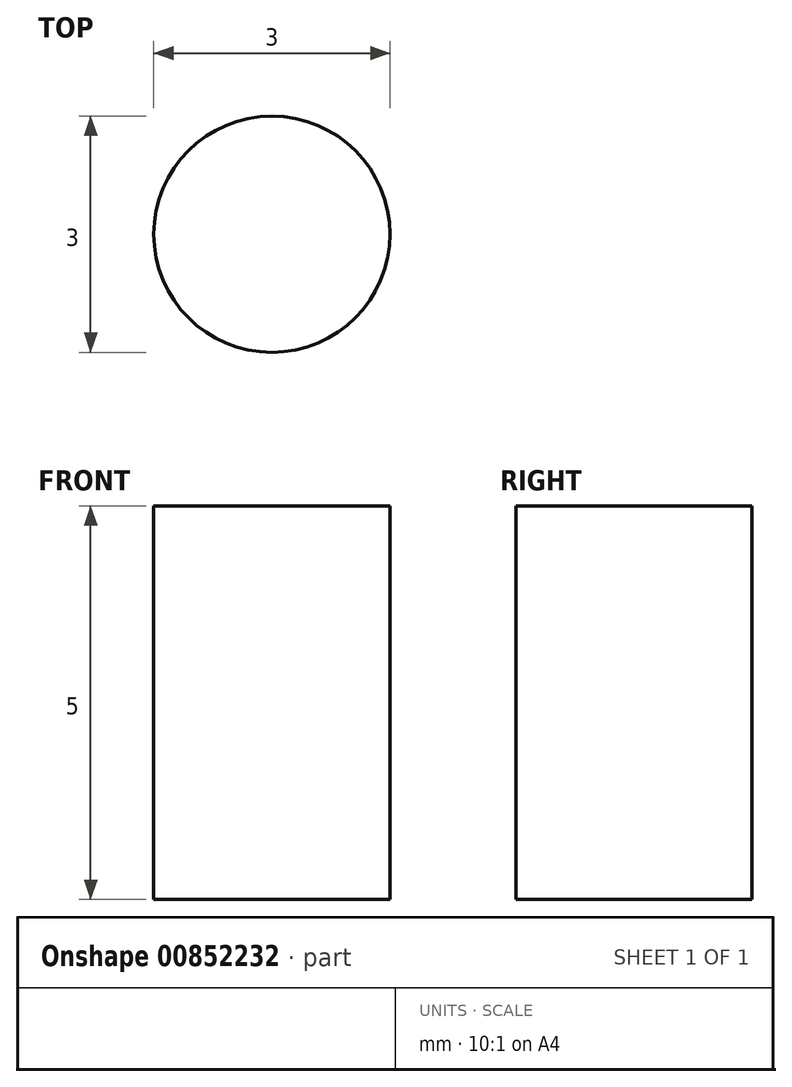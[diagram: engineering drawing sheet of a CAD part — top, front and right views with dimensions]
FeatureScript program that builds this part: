
annotation { "Feature Type Name" : "Feature", "Feature Type Description" : "" }
export const myFeature = defineFeature(function(context is Context, id is Id, definition is map)
    precondition{}
    {
        {
            var Q0;
            Q0=qCreatedBy(makeId("Top.planeOp"),FACE);
            var sketch = newSketch(context, id + "F0", { "sketchPlane" : qUnion([Q0])});
            skCircle(sketch, "E0", {"center": v(0, 0) * mm, "radius": 27 * mm});
            skSolve(sketch);
        }
        {
            var Q0;
            Q0=makeQuery(id+"F0.imprint","IMPRINT",FACE,{"disambiguationData":[TD([[makeQuery(id+"F0.imprint","IMPRINT",EDGE,{"derivedFrom":sQuery(id+"F0.wireOp",EDGE,"E0")}),1.0]])]});
            extrude(context, id + "F1", {"entities" : qUnion([Q0]), "depth" : 5 * mm, "offsetDistance" : 25 * mm});
        }
        {
            var Q0;
            {var subQ0=sQuery(id+"F37MvCQ3r0wqFin_1.wireOp",EDGE,"f4uybqiO-2By2-jBmk-46SA-pqxdGsBmxj9X");var subQ1=sQuery(id+"F37MvCQ3r0wqFin_1.wireOp",EDGE,"YBS4xQga-kdXz-Xd6Z-IQxe-r2HOvKNWWecW");var subQ3=sQuery(id+"F37MvCQ3r0wqFin_1.wireOp",EDGE,"gupYa68e-aYtB-tSWe-53kB-uYkL865cLbxZ");var subQ4=sQuery(id+"F37MvCQ3r0wqFin_1.wireOp",EDGE,"4d4407c7-a204-4c44-b440-6ebbf1cd7b63.1.0.0");var subQ5=sQuery(id+"F0.wireOp",EDGE,"E0");var subQ6=sQuery(id+"F37MvCQ3r0wqFin_1.wireOp",EDGE,"S5JysFVE-GN5k-qked-gyNs-9rrJIgPoBisO");var subQ8=sQuery(id+"F37MvCQ3r0wqFin_1.wireOp",EDGE,"622e7514-f5f2-47ed-ba9b-ec6ca30ba75c0.MirrorCS");var subQ10=sQuery(id+"F37MvCQ3r0wqFin_1.wireOp",EDGE,"19809d41-3397-4dab-8baa-fab7fa50255a0.MirrorCS");Q0=makeQuery(id+"FV6EzTKN9YXR9Vd_1.boolean.opBoolean","SPLIT",EDGE,{"disambiguationData":[TD([makeQuery(id+"F1.opExtrude","SWEPT_FACE",FACE,{"disambiguationData":[OSD([subQ5])]}),makeQuery(id+"F1.opExtrude","CAP_FACE",FACE,{"disambiguationData":[OSD([subQ5])],"isStart":false}),makeQuery(id+"FV6EzTKN9YXR9Vd_1.opExtrude","SWEPT_FACE",FACE,{"disambiguationData":[OSD([subQ1]),TDD([makeQuery(id+"F37MvCQ3r0wqFin_1.imprint","IMPRINT",EDGE,{"disambiguationData":[TD([[makeQuery(id+"F37MvCQ3r0wqFin_1.imprint","INTERSECT",VERTEX,{"disambiguationData":[OD(0.0)],"derivedFrom":[subQ1,subQ10]}),1.0]])],"derivedFrom":subQ1})])]}),makeQuery(id+"FV6EzTKN9YXR9Vd_1.opExtrude","SWEPT_FACE",FACE,{"disambiguationData":[OSD([subQ1]),TDD([makeQuery(id+"F37MvCQ3r0wqFin_1.imprint","IMPRINT",EDGE,{"disambiguationData":[TD([[makeQuery(id+"F37MvCQ3r0wqFin_1.imprint","INTERSECT",VERTEX,{"disambiguationData":[OD(0.0)],"derivedFrom":[subQ1,subQ8]}),1.0]])],"derivedFrom":subQ1})])]}),makeQuery(id+"FV6EzTKN9YXR9Vd_1.opExtrude","SWEPT_FACE",FACE,{"disambiguationData":[OSD([subQ1]),TDD([makeQuery(id+"F37MvCQ3r0wqFin_1.imprint","IMPRINT",EDGE,{"disambiguationData":[TD([[makeQuery(id+"F37MvCQ3r0wqFin_1.imprint","INTERSECT",VERTEX,{"disambiguationData":[OD(0.0)],"derivedFrom":[subQ1,subQ6]}),1.0]])],"derivedFrom":subQ1})])]}),makeQuery(id+"FV6EzTKN9YXR9Vd_1.opExtrude","SWEPT_FACE",FACE,{"disambiguationData":[OSD([subQ1]),TDD([makeQuery(id+"F37MvCQ3r0wqFin_1.imprint","IMPRINT",EDGE,{"disambiguationData":[TD([[makeQuery(id+"F37MvCQ3r0wqFin_1.imprint","INTERSECT",VERTEX,{"disambiguationData":[OD(0.0)],"derivedFrom":[subQ1,subQ0]}),-1.0]])],"derivedFrom":subQ1})])]}),makeQuery(id+"FV6EzTKN9YXR9Vd_1.opExtrude","SWEPT_FACE",FACE,{"disambiguationData":[OSD([subQ1]),TDD([makeQuery(id+"F37MvCQ3r0wqFin_1.imprint","IMPRINT",EDGE,{"disambiguationData":[TD([[makeQuery(id+"F37MvCQ3r0wqFin_1.imprint","INTERSECT",VERTEX,{"disambiguationData":[OD(0.0)],"derivedFrom":[subQ1,subQ3]}),-1.0]])],"derivedFrom":subQ1})])]}),makeQuery(id+"FV6EzTKN9YXR9Vd_1.opExtrude","SWEPT_FACE",FACE,{"disambiguationData":[OSD([subQ1]),TDD([makeQuery(id+"F37MvCQ3r0wqFin_1.imprint","IMPRINT",EDGE,{"disambiguationData":[TD([[makeQuery(id+"F37MvCQ3r0wqFin_1.imprint","INTERSECT",VERTEX,{"disambiguationData":[OD(1.0)],"derivedFrom":[subQ1,subQ3]}),1.0]])],"derivedFrom":subQ1})])]}),makeQuery(id+"FV6EzTKN9YXR9Vd_1.opExtrude","SWEPT_FACE",FACE,{"disambiguationData":[OSD([subQ1]),TDD([makeQuery(id+"F37MvCQ3r0wqFin_1.imprint","IMPRINT",EDGE,{"disambiguationData":[TD([[makeQuery(id+"F37MvCQ3r0wqFin_1.imprint","INTERSECT",VERTEX,{"disambiguationData":[OD(1.0)],"derivedFrom":[subQ1,subQ0]}),1.0]])],"derivedFrom":subQ1})])]}),makeQuery(id+"FV6EzTKN9YXR9Vd_1.opExtrude","SWEPT_FACE",FACE,{"disambiguationData":[OSD([subQ1]),TDD([makeQuery(id+"F37MvCQ3r0wqFin_1.imprint","IMPRINT",EDGE,{"disambiguationData":[TD([[makeQuery(id+"F37MvCQ3r0wqFin_1.imprint","INTERSECT",VERTEX,{"disambiguationData":[OD(1.0)],"derivedFrom":[subQ1,subQ6]}),-1.0]])],"derivedFrom":subQ1})])]}),makeQuery(id+"FV6EzTKN9YXR9Vd_1.opExtrude","SWEPT_FACE",FACE,{"disambiguationData":[OSD([subQ1]),TDD([makeQuery(id+"F37MvCQ3r0wqFin_1.imprint","IMPRINT",EDGE,{"disambiguationData":[TD([[makeQuery(id+"F37MvCQ3r0wqFin_1.imprint","INTERSECT",VERTEX,{"disambiguationData":[OD(1.0)],"derivedFrom":[subQ1,subQ8]}),-1.0]])],"derivedFrom":subQ1})])]}),makeQuery(id+"FV6EzTKN9YXR9Vd_1.opExtrude","SWEPT_FACE",FACE,{"disambiguationData":[OSD([subQ1]),TDD([makeQuery(id+"F37MvCQ3r0wqFin_1.imprint","IMPRINT",EDGE,{"disambiguationData":[TD([[makeQuery(id+"F37MvCQ3r0wqFin_1.imprint","INTERSECT",VERTEX,{"disambiguationData":[OD(1.0)],"derivedFrom":[subQ1,subQ10]}),-1.0]])],"derivedFrom":subQ1})])]}),makeQuery(id+"FV6EzTKN9YXR9Vd_1.opExtrude","SWEPT_FACE",FACE,{"disambiguationData":[OSD([subQ4])]})])],"derivedFrom":makeQuery(id+"F1.opExtrude","CAP_EDGE",EDGE,{"disambiguationData":[OSD([subQ5])],"isStart":false})});}
            var Q1;
            {var subQ0=sQuery(id+"F37MvCQ3r0wqFin_1.wireOp",EDGE,"f4uybqiO-2By2-jBmk-46SA-pqxdGsBmxj9X");var subQ1=sQuery(id+"F37MvCQ3r0wqFin_1.wireOp",EDGE,"YBS4xQga-kdXz-Xd6Z-IQxe-r2HOvKNWWecW");var subQ2=sQuery(id+"F37MvCQ3r0wqFin_1.wireOp",EDGE,"x8pBDlyB-b0kH-kFwn-oj1M-qMSimfXZpj5B");var subQ3=sQuery(id+"F37MvCQ3r0wqFin_1.wireOp",EDGE,"gupYa68e-aYtB-tSWe-53kB-uYkL865cLbxZ");var subQ5=sQuery(id+"F0.wireOp",EDGE,"E0");var subQ6=sQuery(id+"F37MvCQ3r0wqFin_1.wireOp",EDGE,"S5JysFVE-GN5k-qked-gyNs-9rrJIgPoBisO");var subQ8=sQuery(id+"F37MvCQ3r0wqFin_1.wireOp",EDGE,"622e7514-f5f2-47ed-ba9b-ec6ca30ba75c0.MirrorCS");var subQ10=sQuery(id+"F37MvCQ3r0wqFin_1.wireOp",EDGE,"19809d41-3397-4dab-8baa-fab7fa50255a0.MirrorCS");Q1=makeQuery(id+"FV6EzTKN9YXR9Vd_1.boolean.opBoolean","SPLIT",EDGE,{"disambiguationData":[TD([makeQuery(id+"F1.opExtrude","SWEPT_FACE",FACE,{"disambiguationData":[OSD([subQ5])]}),makeQuery(id+"F1.opExtrude","CAP_FACE",FACE,{"disambiguationData":[OSD([subQ5])],"isStart":false}),makeQuery(id+"FV6EzTKN9YXR9Vd_1.opExtrude","SWEPT_FACE",FACE,{"disambiguationData":[OSD([subQ1]),TDD([makeQuery(id+"F37MvCQ3r0wqFin_1.imprint","IMPRINT",EDGE,{"disambiguationData":[TD([[makeQuery(id+"F37MvCQ3r0wqFin_1.imprint","INTERSECT",VERTEX,{"disambiguationData":[OD(0.0)],"derivedFrom":[subQ1,subQ10]}),1.0]])],"derivedFrom":subQ1})])]}),makeQuery(id+"FV6EzTKN9YXR9Vd_1.opExtrude","SWEPT_FACE",FACE,{"disambiguationData":[OSD([subQ1]),TDD([makeQuery(id+"F37MvCQ3r0wqFin_1.imprint","IMPRINT",EDGE,{"disambiguationData":[TD([[makeQuery(id+"F37MvCQ3r0wqFin_1.imprint","INTERSECT",VERTEX,{"disambiguationData":[OD(0.0)],"derivedFrom":[subQ1,subQ8]}),1.0]])],"derivedFrom":subQ1})])]}),makeQuery(id+"FV6EzTKN9YXR9Vd_1.opExtrude","SWEPT_FACE",FACE,{"disambiguationData":[OSD([subQ1]),TDD([makeQuery(id+"F37MvCQ3r0wqFin_1.imprint","IMPRINT",EDGE,{"disambiguationData":[TD([[makeQuery(id+"F37MvCQ3r0wqFin_1.imprint","INTERSECT",VERTEX,{"disambiguationData":[OD(0.0)],"derivedFrom":[subQ1,subQ6]}),1.0]])],"derivedFrom":subQ1})])]}),makeQuery(id+"FV6EzTKN9YXR9Vd_1.opExtrude","SWEPT_FACE",FACE,{"disambiguationData":[OSD([subQ1]),TDD([makeQuery(id+"F37MvCQ3r0wqFin_1.imprint","IMPRINT",EDGE,{"disambiguationData":[TD([[makeQuery(id+"F37MvCQ3r0wqFin_1.imprint","INTERSECT",VERTEX,{"disambiguationData":[OD(0.0)],"derivedFrom":[subQ1,subQ0]}),-1.0]])],"derivedFrom":subQ1})])]}),makeQuery(id+"FV6EzTKN9YXR9Vd_1.opExtrude","SWEPT_FACE",FACE,{"disambiguationData":[OSD([subQ1]),TDD([makeQuery(id+"F37MvCQ3r0wqFin_1.imprint","IMPRINT",EDGE,{"disambiguationData":[TD([[makeQuery(id+"F37MvCQ3r0wqFin_1.imprint","INTERSECT",VERTEX,{"disambiguationData":[OD(0.0)],"derivedFrom":[subQ1,subQ3]}),-1.0]])],"derivedFrom":subQ1})])]}),makeQuery(id+"FV6EzTKN9YXR9Vd_1.opExtrude","SWEPT_FACE",FACE,{"disambiguationData":[OSD([subQ1]),TDD([makeQuery(id+"F37MvCQ3r0wqFin_1.imprint","IMPRINT",EDGE,{"disambiguationData":[TD([[makeQuery(id+"F37MvCQ3r0wqFin_1.imprint","INTERSECT",VERTEX,{"disambiguationData":[OD(1.0)],"derivedFrom":[subQ1,subQ3]}),1.0]])],"derivedFrom":subQ1})])]}),makeQuery(id+"FV6EzTKN9YXR9Vd_1.opExtrude","SWEPT_FACE",FACE,{"disambiguationData":[OSD([subQ1]),TDD([makeQuery(id+"F37MvCQ3r0wqFin_1.imprint","IMPRINT",EDGE,{"disambiguationData":[TD([[makeQuery(id+"F37MvCQ3r0wqFin_1.imprint","INTERSECT",VERTEX,{"disambiguationData":[OD(1.0)],"derivedFrom":[subQ1,subQ0]}),1.0]])],"derivedFrom":subQ1})])]}),makeQuery(id+"FV6EzTKN9YXR9Vd_1.opExtrude","SWEPT_FACE",FACE,{"disambiguationData":[OSD([subQ1]),TDD([makeQuery(id+"F37MvCQ3r0wqFin_1.imprint","IMPRINT",EDGE,{"disambiguationData":[TD([[makeQuery(id+"F37MvCQ3r0wqFin_1.imprint","INTERSECT",VERTEX,{"disambiguationData":[OD(1.0)],"derivedFrom":[subQ1,subQ6]}),-1.0]])],"derivedFrom":subQ1})])]}),makeQuery(id+"FV6EzTKN9YXR9Vd_1.opExtrude","SWEPT_FACE",FACE,{"disambiguationData":[OSD([subQ1]),TDD([makeQuery(id+"F37MvCQ3r0wqFin_1.imprint","IMPRINT",EDGE,{"disambiguationData":[TD([[makeQuery(id+"F37MvCQ3r0wqFin_1.imprint","INTERSECT",VERTEX,{"disambiguationData":[OD(1.0)],"derivedFrom":[subQ1,subQ8]}),-1.0]])],"derivedFrom":subQ1})])]}),makeQuery(id+"FV6EzTKN9YXR9Vd_1.opExtrude","SWEPT_FACE",FACE,{"disambiguationData":[OSD([subQ1]),TDD([makeQuery(id+"F37MvCQ3r0wqFin_1.imprint","IMPRINT",EDGE,{"disambiguationData":[TD([[makeQuery(id+"F37MvCQ3r0wqFin_1.imprint","INTERSECT",VERTEX,{"disambiguationData":[OD(1.0)],"derivedFrom":[subQ1,subQ10]}),-1.0]])],"derivedFrom":subQ1})])]}),makeQuery(id+"FV6EzTKN9YXR9Vd_1.opExtrude","SWEPT_FACE",FACE,{"disambiguationData":[OSD([subQ2])]}),makeQuery(id+"FV6EzTKN9YXR9Vd_1.opExtrude","SWEPT_FACE",FACE,{"disambiguationData":[OSD([subQ3])]})]),OD(0.0)],"derivedFrom":makeQuery(id+"F1.opExtrude","CAP_EDGE",EDGE,{"disambiguationData":[OSD([subQ5])],"isStart":false})});}
            var Q2;
            {var subQ0=sQuery(id+"F37MvCQ3r0wqFin_1.wireOp",EDGE,"f4uybqiO-2By2-jBmk-46SA-pqxdGsBmxj9X");var subQ1=sQuery(id+"F37MvCQ3r0wqFin_1.wireOp",EDGE,"YBS4xQga-kdXz-Xd6Z-IQxe-r2HOvKNWWecW");var subQ3=sQuery(id+"F37MvCQ3r0wqFin_1.wireOp",EDGE,"gupYa68e-aYtB-tSWe-53kB-uYkL865cLbxZ");var subQ5=sQuery(id+"F0.wireOp",EDGE,"E0");var subQ6=sQuery(id+"F37MvCQ3r0wqFin_1.wireOp",EDGE,"S5JysFVE-GN5k-qked-gyNs-9rrJIgPoBisO");var subQ8=sQuery(id+"F37MvCQ3r0wqFin_1.wireOp",EDGE,"622e7514-f5f2-47ed-ba9b-ec6ca30ba75c0.MirrorCS");var subQ10=sQuery(id+"F37MvCQ3r0wqFin_1.wireOp",EDGE,"19809d41-3397-4dab-8baa-fab7fa50255a0.MirrorCS");Q2=makeQuery(id+"FV6EzTKN9YXR9Vd_1.boolean.opBoolean","SPLIT",EDGE,{"disambiguationData":[TD([makeQuery(id+"F1.opExtrude","SWEPT_FACE",FACE,{"disambiguationData":[OSD([subQ5])]}),makeQuery(id+"F1.opExtrude","CAP_FACE",FACE,{"disambiguationData":[OSD([subQ5])],"isStart":false}),makeQuery(id+"FV6EzTKN9YXR9Vd_1.opExtrude","SWEPT_FACE",FACE,{"disambiguationData":[OSD([subQ1]),TDD([makeQuery(id+"F37MvCQ3r0wqFin_1.imprint","IMPRINT",EDGE,{"disambiguationData":[TD([[makeQuery(id+"F37MvCQ3r0wqFin_1.imprint","INTERSECT",VERTEX,{"disambiguationData":[OD(0.0)],"derivedFrom":[subQ1,subQ10]}),1.0]])],"derivedFrom":subQ1})])]}),makeQuery(id+"FV6EzTKN9YXR9Vd_1.opExtrude","SWEPT_FACE",FACE,{"disambiguationData":[OSD([subQ1]),TDD([makeQuery(id+"F37MvCQ3r0wqFin_1.imprint","IMPRINT",EDGE,{"disambiguationData":[TD([[makeQuery(id+"F37MvCQ3r0wqFin_1.imprint","INTERSECT",VERTEX,{"disambiguationData":[OD(0.0)],"derivedFrom":[subQ1,subQ8]}),1.0]])],"derivedFrom":subQ1})])]}),makeQuery(id+"FV6EzTKN9YXR9Vd_1.opExtrude","SWEPT_FACE",FACE,{"disambiguationData":[OSD([subQ1]),TDD([makeQuery(id+"F37MvCQ3r0wqFin_1.imprint","IMPRINT",EDGE,{"disambiguationData":[TD([[makeQuery(id+"F37MvCQ3r0wqFin_1.imprint","INTERSECT",VERTEX,{"disambiguationData":[OD(0.0)],"derivedFrom":[subQ1,subQ6]}),1.0]])],"derivedFrom":subQ1})])]}),makeQuery(id+"FV6EzTKN9YXR9Vd_1.opExtrude","SWEPT_FACE",FACE,{"disambiguationData":[OSD([subQ1]),TDD([makeQuery(id+"F37MvCQ3r0wqFin_1.imprint","IMPRINT",EDGE,{"disambiguationData":[TD([[makeQuery(id+"F37MvCQ3r0wqFin_1.imprint","INTERSECT",VERTEX,{"disambiguationData":[OD(0.0)],"derivedFrom":[subQ1,subQ0]}),-1.0]])],"derivedFrom":subQ1})])]}),makeQuery(id+"FV6EzTKN9YXR9Vd_1.opExtrude","SWEPT_FACE",FACE,{"disambiguationData":[OSD([subQ1]),TDD([makeQuery(id+"F37MvCQ3r0wqFin_1.imprint","IMPRINT",EDGE,{"disambiguationData":[TD([[makeQuery(id+"F37MvCQ3r0wqFin_1.imprint","INTERSECT",VERTEX,{"disambiguationData":[OD(0.0)],"derivedFrom":[subQ1,subQ3]}),-1.0]])],"derivedFrom":subQ1})])]}),makeQuery(id+"FV6EzTKN9YXR9Vd_1.opExtrude","SWEPT_FACE",FACE,{"disambiguationData":[OSD([subQ1]),TDD([makeQuery(id+"F37MvCQ3r0wqFin_1.imprint","IMPRINT",EDGE,{"disambiguationData":[TD([[makeQuery(id+"F37MvCQ3r0wqFin_1.imprint","INTERSECT",VERTEX,{"disambiguationData":[OD(1.0)],"derivedFrom":[subQ1,subQ3]}),1.0]])],"derivedFrom":subQ1})])]}),makeQuery(id+"FV6EzTKN9YXR9Vd_1.opExtrude","SWEPT_FACE",FACE,{"disambiguationData":[OSD([subQ1]),TDD([makeQuery(id+"F37MvCQ3r0wqFin_1.imprint","IMPRINT",EDGE,{"disambiguationData":[TD([[makeQuery(id+"F37MvCQ3r0wqFin_1.imprint","INTERSECT",VERTEX,{"disambiguationData":[OD(1.0)],"derivedFrom":[subQ1,subQ0]}),1.0]])],"derivedFrom":subQ1})])]}),makeQuery(id+"FV6EzTKN9YXR9Vd_1.opExtrude","SWEPT_FACE",FACE,{"disambiguationData":[OSD([subQ1]),TDD([makeQuery(id+"F37MvCQ3r0wqFin_1.imprint","IMPRINT",EDGE,{"disambiguationData":[TD([[makeQuery(id+"F37MvCQ3r0wqFin_1.imprint","INTERSECT",VERTEX,{"disambiguationData":[OD(1.0)],"derivedFrom":[subQ1,subQ6]}),-1.0]])],"derivedFrom":subQ1})])]}),makeQuery(id+"FV6EzTKN9YXR9Vd_1.opExtrude","SWEPT_FACE",FACE,{"disambiguationData":[OSD([subQ1]),TDD([makeQuery(id+"F37MvCQ3r0wqFin_1.imprint","IMPRINT",EDGE,{"disambiguationData":[TD([[makeQuery(id+"F37MvCQ3r0wqFin_1.imprint","INTERSECT",VERTEX,{"disambiguationData":[OD(1.0)],"derivedFrom":[subQ1,subQ8]}),-1.0]])],"derivedFrom":subQ1})])]}),makeQuery(id+"FV6EzTKN9YXR9Vd_1.opExtrude","SWEPT_FACE",FACE,{"disambiguationData":[OSD([subQ1]),TDD([makeQuery(id+"F37MvCQ3r0wqFin_1.imprint","IMPRINT",EDGE,{"disambiguationData":[TD([[makeQuery(id+"F37MvCQ3r0wqFin_1.imprint","INTERSECT",VERTEX,{"disambiguationData":[OD(1.0)],"derivedFrom":[subQ1,subQ10]}),-1.0]])],"derivedFrom":subQ1})])]}),makeQuery(id+"FV6EzTKN9YXR9Vd_1.opExtrude","SWEPT_FACE",FACE,{"disambiguationData":[OSD([subQ6])]}),makeQuery(id+"FV6EzTKN9YXR9Vd_1.opExtrude","SWEPT_FACE",FACE,{"disambiguationData":[OSD([subQ0])]})]),OD(0.0)],"derivedFrom":makeQuery(id+"F1.opExtrude","CAP_EDGE",EDGE,{"disambiguationData":[OSD([subQ5])],"isStart":false})});}
            var Q3;
            {var subQ0=sQuery(id+"F37MvCQ3r0wqFin_1.wireOp",EDGE,"f4uybqiO-2By2-jBmk-46SA-pqxdGsBmxj9X");var subQ1=sQuery(id+"F37MvCQ3r0wqFin_1.wireOp",EDGE,"YBS4xQga-kdXz-Xd6Z-IQxe-r2HOvKNWWecW");var subQ3=sQuery(id+"F37MvCQ3r0wqFin_1.wireOp",EDGE,"gupYa68e-aYtB-tSWe-53kB-uYkL865cLbxZ");var subQ5=sQuery(id+"F0.wireOp",EDGE,"E0");var subQ6=sQuery(id+"F37MvCQ3r0wqFin_1.wireOp",EDGE,"S5JysFVE-GN5k-qked-gyNs-9rrJIgPoBisO");var subQ7=sQuery(id+"F37MvCQ3r0wqFin_1.wireOp",EDGE,"8e0f64e6-6478-45b3-90fc-85676b1debbc0.MirrorCS");var subQ8=sQuery(id+"F37MvCQ3r0wqFin_1.wireOp",EDGE,"622e7514-f5f2-47ed-ba9b-ec6ca30ba75c0.MirrorCS");var subQ10=sQuery(id+"F37MvCQ3r0wqFin_1.wireOp",EDGE,"19809d41-3397-4dab-8baa-fab7fa50255a0.MirrorCS");Q3=makeQuery(id+"FV6EzTKN9YXR9Vd_1.boolean.opBoolean","SPLIT",EDGE,{"disambiguationData":[TD([makeQuery(id+"F1.opExtrude","SWEPT_FACE",FACE,{"disambiguationData":[OSD([subQ5])]}),makeQuery(id+"F1.opExtrude","CAP_FACE",FACE,{"disambiguationData":[OSD([subQ5])],"isStart":false}),makeQuery(id+"FV6EzTKN9YXR9Vd_1.opExtrude","SWEPT_FACE",FACE,{"disambiguationData":[OSD([subQ1]),TDD([makeQuery(id+"F37MvCQ3r0wqFin_1.imprint","IMPRINT",EDGE,{"disambiguationData":[TD([[makeQuery(id+"F37MvCQ3r0wqFin_1.imprint","INTERSECT",VERTEX,{"disambiguationData":[OD(0.0)],"derivedFrom":[subQ1,subQ10]}),1.0]])],"derivedFrom":subQ1})])]}),makeQuery(id+"FV6EzTKN9YXR9Vd_1.opExtrude","SWEPT_FACE",FACE,{"disambiguationData":[OSD([subQ1]),TDD([makeQuery(id+"F37MvCQ3r0wqFin_1.imprint","IMPRINT",EDGE,{"disambiguationData":[TD([[makeQuery(id+"F37MvCQ3r0wqFin_1.imprint","INTERSECT",VERTEX,{"disambiguationData":[OD(0.0)],"derivedFrom":[subQ1,subQ8]}),1.0]])],"derivedFrom":subQ1})])]}),makeQuery(id+"FV6EzTKN9YXR9Vd_1.opExtrude","SWEPT_FACE",FACE,{"disambiguationData":[OSD([subQ1]),TDD([makeQuery(id+"F37MvCQ3r0wqFin_1.imprint","IMPRINT",EDGE,{"disambiguationData":[TD([[makeQuery(id+"F37MvCQ3r0wqFin_1.imprint","INTERSECT",VERTEX,{"disambiguationData":[OD(0.0)],"derivedFrom":[subQ1,subQ6]}),1.0]])],"derivedFrom":subQ1})])]}),makeQuery(id+"FV6EzTKN9YXR9Vd_1.opExtrude","SWEPT_FACE",FACE,{"disambiguationData":[OSD([subQ1]),TDD([makeQuery(id+"F37MvCQ3r0wqFin_1.imprint","IMPRINT",EDGE,{"disambiguationData":[TD([[makeQuery(id+"F37MvCQ3r0wqFin_1.imprint","INTERSECT",VERTEX,{"disambiguationData":[OD(0.0)],"derivedFrom":[subQ1,subQ0]}),-1.0]])],"derivedFrom":subQ1})])]}),makeQuery(id+"FV6EzTKN9YXR9Vd_1.opExtrude","SWEPT_FACE",FACE,{"disambiguationData":[OSD([subQ1]),TDD([makeQuery(id+"F37MvCQ3r0wqFin_1.imprint","IMPRINT",EDGE,{"disambiguationData":[TD([[makeQuery(id+"F37MvCQ3r0wqFin_1.imprint","INTERSECT",VERTEX,{"disambiguationData":[OD(0.0)],"derivedFrom":[subQ1,subQ3]}),-1.0]])],"derivedFrom":subQ1})])]}),makeQuery(id+"FV6EzTKN9YXR9Vd_1.opExtrude","SWEPT_FACE",FACE,{"disambiguationData":[OSD([subQ1]),TDD([makeQuery(id+"F37MvCQ3r0wqFin_1.imprint","IMPRINT",EDGE,{"disambiguationData":[TD([[makeQuery(id+"F37MvCQ3r0wqFin_1.imprint","INTERSECT",VERTEX,{"disambiguationData":[OD(1.0)],"derivedFrom":[subQ1,subQ3]}),1.0]])],"derivedFrom":subQ1})])]}),makeQuery(id+"FV6EzTKN9YXR9Vd_1.opExtrude","SWEPT_FACE",FACE,{"disambiguationData":[OSD([subQ1]),TDD([makeQuery(id+"F37MvCQ3r0wqFin_1.imprint","IMPRINT",EDGE,{"disambiguationData":[TD([[makeQuery(id+"F37MvCQ3r0wqFin_1.imprint","INTERSECT",VERTEX,{"disambiguationData":[OD(1.0)],"derivedFrom":[subQ1,subQ0]}),1.0]])],"derivedFrom":subQ1})])]}),makeQuery(id+"FV6EzTKN9YXR9Vd_1.opExtrude","SWEPT_FACE",FACE,{"disambiguationData":[OSD([subQ1]),TDD([makeQuery(id+"F37MvCQ3r0wqFin_1.imprint","IMPRINT",EDGE,{"disambiguationData":[TD([[makeQuery(id+"F37MvCQ3r0wqFin_1.imprint","INTERSECT",VERTEX,{"disambiguationData":[OD(1.0)],"derivedFrom":[subQ1,subQ6]}),-1.0]])],"derivedFrom":subQ1})])]}),makeQuery(id+"FV6EzTKN9YXR9Vd_1.opExtrude","SWEPT_FACE",FACE,{"disambiguationData":[OSD([subQ1]),TDD([makeQuery(id+"F37MvCQ3r0wqFin_1.imprint","IMPRINT",EDGE,{"disambiguationData":[TD([[makeQuery(id+"F37MvCQ3r0wqFin_1.imprint","INTERSECT",VERTEX,{"disambiguationData":[OD(1.0)],"derivedFrom":[subQ1,subQ8]}),-1.0]])],"derivedFrom":subQ1})])]}),makeQuery(id+"FV6EzTKN9YXR9Vd_1.opExtrude","SWEPT_FACE",FACE,{"disambiguationData":[OSD([subQ1]),TDD([makeQuery(id+"F37MvCQ3r0wqFin_1.imprint","IMPRINT",EDGE,{"disambiguationData":[TD([[makeQuery(id+"F37MvCQ3r0wqFin_1.imprint","INTERSECT",VERTEX,{"disambiguationData":[OD(1.0)],"derivedFrom":[subQ1,subQ10]}),-1.0]])],"derivedFrom":subQ1})])]}),makeQuery(id+"FV6EzTKN9YXR9Vd_1.opExtrude","SWEPT_FACE",FACE,{"disambiguationData":[OSD([subQ7])]}),makeQuery(id+"FV6EzTKN9YXR9Vd_1.opExtrude","SWEPT_FACE",FACE,{"disambiguationData":[OSD([subQ8])]})]),OD(0.0)],"derivedFrom":makeQuery(id+"F1.opExtrude","CAP_EDGE",EDGE,{"disambiguationData":[OSD([subQ5])],"isStart":false})});}
            var Q4;
            {var subQ0=sQuery(id+"F37MvCQ3r0wqFin_1.wireOp",EDGE,"f4uybqiO-2By2-jBmk-46SA-pqxdGsBmxj9X");var subQ1=sQuery(id+"F37MvCQ3r0wqFin_1.wireOp",EDGE,"YBS4xQga-kdXz-Xd6Z-IQxe-r2HOvKNWWecW");var subQ3=sQuery(id+"F37MvCQ3r0wqFin_1.wireOp",EDGE,"gupYa68e-aYtB-tSWe-53kB-uYkL865cLbxZ");var subQ5=sQuery(id+"F0.wireOp",EDGE,"E0");var subQ6=sQuery(id+"F37MvCQ3r0wqFin_1.wireOp",EDGE,"S5JysFVE-GN5k-qked-gyNs-9rrJIgPoBisO");var subQ8=sQuery(id+"F37MvCQ3r0wqFin_1.wireOp",EDGE,"622e7514-f5f2-47ed-ba9b-ec6ca30ba75c0.MirrorCS");var subQ9=sQuery(id+"F37MvCQ3r0wqFin_1.wireOp",EDGE,"5de1f45e-9a1b-4934-bea5-5e23e1e5ec5c0.MirrorCS");var subQ10=sQuery(id+"F37MvCQ3r0wqFin_1.wireOp",EDGE,"19809d41-3397-4dab-8baa-fab7fa50255a0.MirrorCS");Q4=makeQuery(id+"FV6EzTKN9YXR9Vd_1.boolean.opBoolean","SPLIT",EDGE,{"disambiguationData":[TD([makeQuery(id+"F1.opExtrude","SWEPT_FACE",FACE,{"disambiguationData":[OSD([subQ5])]}),makeQuery(id+"F1.opExtrude","CAP_FACE",FACE,{"disambiguationData":[OSD([subQ5])],"isStart":false}),makeQuery(id+"FV6EzTKN9YXR9Vd_1.opExtrude","SWEPT_FACE",FACE,{"disambiguationData":[OSD([subQ1]),TDD([makeQuery(id+"F37MvCQ3r0wqFin_1.imprint","IMPRINT",EDGE,{"disambiguationData":[TD([[makeQuery(id+"F37MvCQ3r0wqFin_1.imprint","INTERSECT",VERTEX,{"disambiguationData":[OD(0.0)],"derivedFrom":[subQ1,subQ10]}),1.0]])],"derivedFrom":subQ1})])]}),makeQuery(id+"FV6EzTKN9YXR9Vd_1.opExtrude","SWEPT_FACE",FACE,{"disambiguationData":[OSD([subQ1]),TDD([makeQuery(id+"F37MvCQ3r0wqFin_1.imprint","IMPRINT",EDGE,{"disambiguationData":[TD([[makeQuery(id+"F37MvCQ3r0wqFin_1.imprint","INTERSECT",VERTEX,{"disambiguationData":[OD(0.0)],"derivedFrom":[subQ1,subQ8]}),1.0]])],"derivedFrom":subQ1})])]}),makeQuery(id+"FV6EzTKN9YXR9Vd_1.opExtrude","SWEPT_FACE",FACE,{"disambiguationData":[OSD([subQ1]),TDD([makeQuery(id+"F37MvCQ3r0wqFin_1.imprint","IMPRINT",EDGE,{"disambiguationData":[TD([[makeQuery(id+"F37MvCQ3r0wqFin_1.imprint","INTERSECT",VERTEX,{"disambiguationData":[OD(0.0)],"derivedFrom":[subQ1,subQ6]}),1.0]])],"derivedFrom":subQ1})])]}),makeQuery(id+"FV6EzTKN9YXR9Vd_1.opExtrude","SWEPT_FACE",FACE,{"disambiguationData":[OSD([subQ1]),TDD([makeQuery(id+"F37MvCQ3r0wqFin_1.imprint","IMPRINT",EDGE,{"disambiguationData":[TD([[makeQuery(id+"F37MvCQ3r0wqFin_1.imprint","INTERSECT",VERTEX,{"disambiguationData":[OD(0.0)],"derivedFrom":[subQ1,subQ0]}),-1.0]])],"derivedFrom":subQ1})])]}),makeQuery(id+"FV6EzTKN9YXR9Vd_1.opExtrude","SWEPT_FACE",FACE,{"disambiguationData":[OSD([subQ1]),TDD([makeQuery(id+"F37MvCQ3r0wqFin_1.imprint","IMPRINT",EDGE,{"disambiguationData":[TD([[makeQuery(id+"F37MvCQ3r0wqFin_1.imprint","INTERSECT",VERTEX,{"disambiguationData":[OD(0.0)],"derivedFrom":[subQ1,subQ3]}),-1.0]])],"derivedFrom":subQ1})])]}),makeQuery(id+"FV6EzTKN9YXR9Vd_1.opExtrude","SWEPT_FACE",FACE,{"disambiguationData":[OSD([subQ1]),TDD([makeQuery(id+"F37MvCQ3r0wqFin_1.imprint","IMPRINT",EDGE,{"disambiguationData":[TD([[makeQuery(id+"F37MvCQ3r0wqFin_1.imprint","INTERSECT",VERTEX,{"disambiguationData":[OD(1.0)],"derivedFrom":[subQ1,subQ3]}),1.0]])],"derivedFrom":subQ1})])]}),makeQuery(id+"FV6EzTKN9YXR9Vd_1.opExtrude","SWEPT_FACE",FACE,{"disambiguationData":[OSD([subQ1]),TDD([makeQuery(id+"F37MvCQ3r0wqFin_1.imprint","IMPRINT",EDGE,{"disambiguationData":[TD([[makeQuery(id+"F37MvCQ3r0wqFin_1.imprint","INTERSECT",VERTEX,{"disambiguationData":[OD(1.0)],"derivedFrom":[subQ1,subQ0]}),1.0]])],"derivedFrom":subQ1})])]}),makeQuery(id+"FV6EzTKN9YXR9Vd_1.opExtrude","SWEPT_FACE",FACE,{"disambiguationData":[OSD([subQ1]),TDD([makeQuery(id+"F37MvCQ3r0wqFin_1.imprint","IMPRINT",EDGE,{"disambiguationData":[TD([[makeQuery(id+"F37MvCQ3r0wqFin_1.imprint","INTERSECT",VERTEX,{"disambiguationData":[OD(1.0)],"derivedFrom":[subQ1,subQ6]}),-1.0]])],"derivedFrom":subQ1})])]}),makeQuery(id+"FV6EzTKN9YXR9Vd_1.opExtrude","SWEPT_FACE",FACE,{"disambiguationData":[OSD([subQ1]),TDD([makeQuery(id+"F37MvCQ3r0wqFin_1.imprint","IMPRINT",EDGE,{"disambiguationData":[TD([[makeQuery(id+"F37MvCQ3r0wqFin_1.imprint","INTERSECT",VERTEX,{"disambiguationData":[OD(1.0)],"derivedFrom":[subQ1,subQ8]}),-1.0]])],"derivedFrom":subQ1})])]}),makeQuery(id+"FV6EzTKN9YXR9Vd_1.opExtrude","SWEPT_FACE",FACE,{"disambiguationData":[OSD([subQ1]),TDD([makeQuery(id+"F37MvCQ3r0wqFin_1.imprint","IMPRINT",EDGE,{"disambiguationData":[TD([[makeQuery(id+"F37MvCQ3r0wqFin_1.imprint","INTERSECT",VERTEX,{"disambiguationData":[OD(1.0)],"derivedFrom":[subQ1,subQ10]}),-1.0]])],"derivedFrom":subQ1})])]}),makeQuery(id+"FV6EzTKN9YXR9Vd_1.opExtrude","SWEPT_FACE",FACE,{"disambiguationData":[OSD([subQ9])]}),makeQuery(id+"FV6EzTKN9YXR9Vd_1.opExtrude","SWEPT_FACE",FACE,{"disambiguationData":[OSD([subQ10])]})]),OD(0.0)],"derivedFrom":makeQuery(id+"F1.opExtrude","CAP_EDGE",EDGE,{"disambiguationData":[OSD([subQ5])],"isStart":false})});}
            var Q5;
            {var subQ0=sQuery(id+"F37MvCQ3r0wqFin_1.wireOp",EDGE,"f4uybqiO-2By2-jBmk-46SA-pqxdGsBmxj9X");var subQ1=sQuery(id+"F37MvCQ3r0wqFin_1.wireOp",EDGE,"YBS4xQga-kdXz-Xd6Z-IQxe-r2HOvKNWWecW");var subQ3=sQuery(id+"F37MvCQ3r0wqFin_1.wireOp",EDGE,"gupYa68e-aYtB-tSWe-53kB-uYkL865cLbxZ");var subQ5=sQuery(id+"F0.wireOp",EDGE,"E0");var subQ6=sQuery(id+"F37MvCQ3r0wqFin_1.wireOp",EDGE,"S5JysFVE-GN5k-qked-gyNs-9rrJIgPoBisO");var subQ8=sQuery(id+"F37MvCQ3r0wqFin_1.wireOp",EDGE,"e7f0d98c-08e8-46b2-a157-88f89b1725ea0.MirrorCS");var subQ9=sQuery(id+"F37MvCQ3r0wqFin_1.wireOp",EDGE,"622e7514-f5f2-47ed-ba9b-ec6ca30ba75c0.MirrorCS");var subQ11=sQuery(id+"F37MvCQ3r0wqFin_1.wireOp",EDGE,"19809d41-3397-4dab-8baa-fab7fa50255a0.MirrorCS");Q5=makeQuery(id+"FV6EzTKN9YXR9Vd_1.boolean.opBoolean","SPLIT",EDGE,{"disambiguationData":[TD([makeQuery(id+"F1.opExtrude","SWEPT_FACE",FACE,{"disambiguationData":[OSD([subQ5])]}),makeQuery(id+"F1.opExtrude","CAP_FACE",FACE,{"disambiguationData":[OSD([subQ5])],"isStart":false}),makeQuery(id+"FV6EzTKN9YXR9Vd_1.opExtrude","SWEPT_FACE",FACE,{"disambiguationData":[OSD([subQ1]),TDD([makeQuery(id+"F37MvCQ3r0wqFin_1.imprint","IMPRINT",EDGE,{"disambiguationData":[TD([[makeQuery(id+"F37MvCQ3r0wqFin_1.imprint","INTERSECT",VERTEX,{"disambiguationData":[OD(0.0)],"derivedFrom":[subQ1,subQ11]}),1.0]])],"derivedFrom":subQ1})])]}),makeQuery(id+"FV6EzTKN9YXR9Vd_1.opExtrude","SWEPT_FACE",FACE,{"disambiguationData":[OSD([subQ1]),TDD([makeQuery(id+"F37MvCQ3r0wqFin_1.imprint","IMPRINT",EDGE,{"disambiguationData":[TD([[makeQuery(id+"F37MvCQ3r0wqFin_1.imprint","INTERSECT",VERTEX,{"disambiguationData":[OD(0.0)],"derivedFrom":[subQ1,subQ9]}),1.0]])],"derivedFrom":subQ1})])]}),makeQuery(id+"FV6EzTKN9YXR9Vd_1.opExtrude","SWEPT_FACE",FACE,{"disambiguationData":[OSD([subQ1]),TDD([makeQuery(id+"F37MvCQ3r0wqFin_1.imprint","IMPRINT",EDGE,{"disambiguationData":[TD([[makeQuery(id+"F37MvCQ3r0wqFin_1.imprint","INTERSECT",VERTEX,{"disambiguationData":[OD(0.0)],"derivedFrom":[subQ1,subQ6]}),1.0]])],"derivedFrom":subQ1})])]}),makeQuery(id+"FV6EzTKN9YXR9Vd_1.opExtrude","SWEPT_FACE",FACE,{"disambiguationData":[OSD([subQ1]),TDD([makeQuery(id+"F37MvCQ3r0wqFin_1.imprint","IMPRINT",EDGE,{"disambiguationData":[TD([[makeQuery(id+"F37MvCQ3r0wqFin_1.imprint","INTERSECT",VERTEX,{"disambiguationData":[OD(0.0)],"derivedFrom":[subQ1,subQ0]}),-1.0]])],"derivedFrom":subQ1})])]}),makeQuery(id+"FV6EzTKN9YXR9Vd_1.opExtrude","SWEPT_FACE",FACE,{"disambiguationData":[OSD([subQ1]),TDD([makeQuery(id+"F37MvCQ3r0wqFin_1.imprint","IMPRINT",EDGE,{"disambiguationData":[TD([[makeQuery(id+"F37MvCQ3r0wqFin_1.imprint","INTERSECT",VERTEX,{"disambiguationData":[OD(0.0)],"derivedFrom":[subQ1,subQ3]}),-1.0]])],"derivedFrom":subQ1})])]}),makeQuery(id+"FV6EzTKN9YXR9Vd_1.opExtrude","SWEPT_FACE",FACE,{"disambiguationData":[OSD([subQ1]),TDD([makeQuery(id+"F37MvCQ3r0wqFin_1.imprint","IMPRINT",EDGE,{"disambiguationData":[TD([[makeQuery(id+"F37MvCQ3r0wqFin_1.imprint","INTERSECT",VERTEX,{"disambiguationData":[OD(1.0)],"derivedFrom":[subQ1,subQ3]}),1.0]])],"derivedFrom":subQ1})])]}),makeQuery(id+"FV6EzTKN9YXR9Vd_1.opExtrude","SWEPT_FACE",FACE,{"disambiguationData":[OSD([subQ1]),TDD([makeQuery(id+"F37MvCQ3r0wqFin_1.imprint","IMPRINT",EDGE,{"disambiguationData":[TD([[makeQuery(id+"F37MvCQ3r0wqFin_1.imprint","INTERSECT",VERTEX,{"disambiguationData":[OD(1.0)],"derivedFrom":[subQ1,subQ0]}),1.0]])],"derivedFrom":subQ1})])]}),makeQuery(id+"FV6EzTKN9YXR9Vd_1.opExtrude","SWEPT_FACE",FACE,{"disambiguationData":[OSD([subQ1]),TDD([makeQuery(id+"F37MvCQ3r0wqFin_1.imprint","IMPRINT",EDGE,{"disambiguationData":[TD([[makeQuery(id+"F37MvCQ3r0wqFin_1.imprint","INTERSECT",VERTEX,{"disambiguationData":[OD(1.0)],"derivedFrom":[subQ1,subQ6]}),-1.0]])],"derivedFrom":subQ1})])]}),makeQuery(id+"FV6EzTKN9YXR9Vd_1.opExtrude","SWEPT_FACE",FACE,{"disambiguationData":[OSD([subQ1]),TDD([makeQuery(id+"F37MvCQ3r0wqFin_1.imprint","IMPRINT",EDGE,{"disambiguationData":[TD([[makeQuery(id+"F37MvCQ3r0wqFin_1.imprint","INTERSECT",VERTEX,{"disambiguationData":[OD(1.0)],"derivedFrom":[subQ1,subQ9]}),-1.0]])],"derivedFrom":subQ1})])]}),makeQuery(id+"FV6EzTKN9YXR9Vd_1.opExtrude","SWEPT_FACE",FACE,{"disambiguationData":[OSD([subQ1]),TDD([makeQuery(id+"F37MvCQ3r0wqFin_1.imprint","IMPRINT",EDGE,{"disambiguationData":[TD([[makeQuery(id+"F37MvCQ3r0wqFin_1.imprint","INTERSECT",VERTEX,{"disambiguationData":[OD(1.0)],"derivedFrom":[subQ1,subQ11]}),-1.0]])],"derivedFrom":subQ1})])]}),makeQuery(id+"FV6EzTKN9YXR9Vd_1.opExtrude","SWEPT_FACE",FACE,{"disambiguationData":[OSD([subQ8])]})])],"derivedFrom":makeQuery(id+"F1.opExtrude","CAP_EDGE",EDGE,{"disambiguationData":[OSD([subQ5])],"isStart":false})});}
            var Q6;
            {var subQ0=sQuery(id+"F37MvCQ3r0wqFin_1.wireOp",EDGE,"f4uybqiO-2By2-jBmk-46SA-pqxdGsBmxj9X");var subQ1=sQuery(id+"F37MvCQ3r0wqFin_1.wireOp",EDGE,"YBS4xQga-kdXz-Xd6Z-IQxe-r2HOvKNWWecW");var subQ3=sQuery(id+"F37MvCQ3r0wqFin_1.wireOp",EDGE,"gupYa68e-aYtB-tSWe-53kB-uYkL865cLbxZ");var subQ5=sQuery(id+"F0.wireOp",EDGE,"E0");var subQ6=sQuery(id+"F37MvCQ3r0wqFin_1.wireOp",EDGE,"S5JysFVE-GN5k-qked-gyNs-9rrJIgPoBisO");var subQ8=sQuery(id+"F37MvCQ3r0wqFin_1.wireOp",EDGE,"622e7514-f5f2-47ed-ba9b-ec6ca30ba75c0.MirrorCS");var subQ9=sQuery(id+"F37MvCQ3r0wqFin_1.wireOp",EDGE,"5de1f45e-9a1b-4934-bea5-5e23e1e5ec5c0.MirrorCS");var subQ10=sQuery(id+"F37MvCQ3r0wqFin_1.wireOp",EDGE,"19809d41-3397-4dab-8baa-fab7fa50255a0.MirrorCS");Q6=makeQuery(id+"FV6EzTKN9YXR9Vd_1.boolean.opBoolean","SPLIT",EDGE,{"disambiguationData":[TD([makeQuery(id+"F1.opExtrude","SWEPT_FACE",FACE,{"disambiguationData":[OSD([subQ5])]}),makeQuery(id+"F1.opExtrude","CAP_FACE",FACE,{"disambiguationData":[OSD([subQ5])],"isStart":false}),makeQuery(id+"FV6EzTKN9YXR9Vd_1.opExtrude","SWEPT_FACE",FACE,{"disambiguationData":[OSD([subQ1]),TDD([makeQuery(id+"F37MvCQ3r0wqFin_1.imprint","IMPRINT",EDGE,{"disambiguationData":[TD([[makeQuery(id+"F37MvCQ3r0wqFin_1.imprint","INTERSECT",VERTEX,{"disambiguationData":[OD(0.0)],"derivedFrom":[subQ1,subQ10]}),1.0]])],"derivedFrom":subQ1})])]}),makeQuery(id+"FV6EzTKN9YXR9Vd_1.opExtrude","SWEPT_FACE",FACE,{"disambiguationData":[OSD([subQ1]),TDD([makeQuery(id+"F37MvCQ3r0wqFin_1.imprint","IMPRINT",EDGE,{"disambiguationData":[TD([[makeQuery(id+"F37MvCQ3r0wqFin_1.imprint","INTERSECT",VERTEX,{"disambiguationData":[OD(0.0)],"derivedFrom":[subQ1,subQ8]}),1.0]])],"derivedFrom":subQ1})])]}),makeQuery(id+"FV6EzTKN9YXR9Vd_1.opExtrude","SWEPT_FACE",FACE,{"disambiguationData":[OSD([subQ1]),TDD([makeQuery(id+"F37MvCQ3r0wqFin_1.imprint","IMPRINT",EDGE,{"disambiguationData":[TD([[makeQuery(id+"F37MvCQ3r0wqFin_1.imprint","INTERSECT",VERTEX,{"disambiguationData":[OD(0.0)],"derivedFrom":[subQ1,subQ6]}),1.0]])],"derivedFrom":subQ1})])]}),makeQuery(id+"FV6EzTKN9YXR9Vd_1.opExtrude","SWEPT_FACE",FACE,{"disambiguationData":[OSD([subQ1]),TDD([makeQuery(id+"F37MvCQ3r0wqFin_1.imprint","IMPRINT",EDGE,{"disambiguationData":[TD([[makeQuery(id+"F37MvCQ3r0wqFin_1.imprint","INTERSECT",VERTEX,{"disambiguationData":[OD(0.0)],"derivedFrom":[subQ1,subQ0]}),-1.0]])],"derivedFrom":subQ1})])]}),makeQuery(id+"FV6EzTKN9YXR9Vd_1.opExtrude","SWEPT_FACE",FACE,{"disambiguationData":[OSD([subQ1]),TDD([makeQuery(id+"F37MvCQ3r0wqFin_1.imprint","IMPRINT",EDGE,{"disambiguationData":[TD([[makeQuery(id+"F37MvCQ3r0wqFin_1.imprint","INTERSECT",VERTEX,{"disambiguationData":[OD(0.0)],"derivedFrom":[subQ1,subQ3]}),-1.0]])],"derivedFrom":subQ1})])]}),makeQuery(id+"FV6EzTKN9YXR9Vd_1.opExtrude","SWEPT_FACE",FACE,{"disambiguationData":[OSD([subQ1]),TDD([makeQuery(id+"F37MvCQ3r0wqFin_1.imprint","IMPRINT",EDGE,{"disambiguationData":[TD([[makeQuery(id+"F37MvCQ3r0wqFin_1.imprint","INTERSECT",VERTEX,{"disambiguationData":[OD(1.0)],"derivedFrom":[subQ1,subQ3]}),1.0]])],"derivedFrom":subQ1})])]}),makeQuery(id+"FV6EzTKN9YXR9Vd_1.opExtrude","SWEPT_FACE",FACE,{"disambiguationData":[OSD([subQ1]),TDD([makeQuery(id+"F37MvCQ3r0wqFin_1.imprint","IMPRINT",EDGE,{"disambiguationData":[TD([[makeQuery(id+"F37MvCQ3r0wqFin_1.imprint","INTERSECT",VERTEX,{"disambiguationData":[OD(1.0)],"derivedFrom":[subQ1,subQ0]}),1.0]])],"derivedFrom":subQ1})])]}),makeQuery(id+"FV6EzTKN9YXR9Vd_1.opExtrude","SWEPT_FACE",FACE,{"disambiguationData":[OSD([subQ1]),TDD([makeQuery(id+"F37MvCQ3r0wqFin_1.imprint","IMPRINT",EDGE,{"disambiguationData":[TD([[makeQuery(id+"F37MvCQ3r0wqFin_1.imprint","INTERSECT",VERTEX,{"disambiguationData":[OD(1.0)],"derivedFrom":[subQ1,subQ6]}),-1.0]])],"derivedFrom":subQ1})])]}),makeQuery(id+"FV6EzTKN9YXR9Vd_1.opExtrude","SWEPT_FACE",FACE,{"disambiguationData":[OSD([subQ1]),TDD([makeQuery(id+"F37MvCQ3r0wqFin_1.imprint","IMPRINT",EDGE,{"disambiguationData":[TD([[makeQuery(id+"F37MvCQ3r0wqFin_1.imprint","INTERSECT",VERTEX,{"disambiguationData":[OD(1.0)],"derivedFrom":[subQ1,subQ8]}),-1.0]])],"derivedFrom":subQ1})])]}),makeQuery(id+"FV6EzTKN9YXR9Vd_1.opExtrude","SWEPT_FACE",FACE,{"disambiguationData":[OSD([subQ1]),TDD([makeQuery(id+"F37MvCQ3r0wqFin_1.imprint","IMPRINT",EDGE,{"disambiguationData":[TD([[makeQuery(id+"F37MvCQ3r0wqFin_1.imprint","INTERSECT",VERTEX,{"disambiguationData":[OD(1.0)],"derivedFrom":[subQ1,subQ10]}),-1.0]])],"derivedFrom":subQ1})])]}),makeQuery(id+"FV6EzTKN9YXR9Vd_1.opExtrude","SWEPT_FACE",FACE,{"disambiguationData":[OSD([subQ9])]}),makeQuery(id+"FV6EzTKN9YXR9Vd_1.opExtrude","SWEPT_FACE",FACE,{"disambiguationData":[OSD([subQ10])]})]),OD(1.0)],"derivedFrom":makeQuery(id+"F1.opExtrude","CAP_EDGE",EDGE,{"disambiguationData":[OSD([subQ5])],"isStart":false})});}
            var Q7;
            {var subQ0=sQuery(id+"F37MvCQ3r0wqFin_1.wireOp",EDGE,"f4uybqiO-2By2-jBmk-46SA-pqxdGsBmxj9X");var subQ1=sQuery(id+"F37MvCQ3r0wqFin_1.wireOp",EDGE,"YBS4xQga-kdXz-Xd6Z-IQxe-r2HOvKNWWecW");var subQ3=sQuery(id+"F37MvCQ3r0wqFin_1.wireOp",EDGE,"gupYa68e-aYtB-tSWe-53kB-uYkL865cLbxZ");var subQ5=sQuery(id+"F0.wireOp",EDGE,"E0");var subQ6=sQuery(id+"F37MvCQ3r0wqFin_1.wireOp",EDGE,"S5JysFVE-GN5k-qked-gyNs-9rrJIgPoBisO");var subQ7=sQuery(id+"F37MvCQ3r0wqFin_1.wireOp",EDGE,"8e0f64e6-6478-45b3-90fc-85676b1debbc0.MirrorCS");var subQ8=sQuery(id+"F37MvCQ3r0wqFin_1.wireOp",EDGE,"622e7514-f5f2-47ed-ba9b-ec6ca30ba75c0.MirrorCS");var subQ10=sQuery(id+"F37MvCQ3r0wqFin_1.wireOp",EDGE,"19809d41-3397-4dab-8baa-fab7fa50255a0.MirrorCS");Q7=makeQuery(id+"FV6EzTKN9YXR9Vd_1.boolean.opBoolean","SPLIT",EDGE,{"disambiguationData":[TD([makeQuery(id+"F1.opExtrude","SWEPT_FACE",FACE,{"disambiguationData":[OSD([subQ5])]}),makeQuery(id+"F1.opExtrude","CAP_FACE",FACE,{"disambiguationData":[OSD([subQ5])],"isStart":false}),makeQuery(id+"FV6EzTKN9YXR9Vd_1.opExtrude","SWEPT_FACE",FACE,{"disambiguationData":[OSD([subQ1]),TDD([makeQuery(id+"F37MvCQ3r0wqFin_1.imprint","IMPRINT",EDGE,{"disambiguationData":[TD([[makeQuery(id+"F37MvCQ3r0wqFin_1.imprint","INTERSECT",VERTEX,{"disambiguationData":[OD(0.0)],"derivedFrom":[subQ1,subQ10]}),1.0]])],"derivedFrom":subQ1})])]}),makeQuery(id+"FV6EzTKN9YXR9Vd_1.opExtrude","SWEPT_FACE",FACE,{"disambiguationData":[OSD([subQ1]),TDD([makeQuery(id+"F37MvCQ3r0wqFin_1.imprint","IMPRINT",EDGE,{"disambiguationData":[TD([[makeQuery(id+"F37MvCQ3r0wqFin_1.imprint","INTERSECT",VERTEX,{"disambiguationData":[OD(0.0)],"derivedFrom":[subQ1,subQ8]}),1.0]])],"derivedFrom":subQ1})])]}),makeQuery(id+"FV6EzTKN9YXR9Vd_1.opExtrude","SWEPT_FACE",FACE,{"disambiguationData":[OSD([subQ1]),TDD([makeQuery(id+"F37MvCQ3r0wqFin_1.imprint","IMPRINT",EDGE,{"disambiguationData":[TD([[makeQuery(id+"F37MvCQ3r0wqFin_1.imprint","INTERSECT",VERTEX,{"disambiguationData":[OD(0.0)],"derivedFrom":[subQ1,subQ6]}),1.0]])],"derivedFrom":subQ1})])]}),makeQuery(id+"FV6EzTKN9YXR9Vd_1.opExtrude","SWEPT_FACE",FACE,{"disambiguationData":[OSD([subQ1]),TDD([makeQuery(id+"F37MvCQ3r0wqFin_1.imprint","IMPRINT",EDGE,{"disambiguationData":[TD([[makeQuery(id+"F37MvCQ3r0wqFin_1.imprint","INTERSECT",VERTEX,{"disambiguationData":[OD(0.0)],"derivedFrom":[subQ1,subQ0]}),-1.0]])],"derivedFrom":subQ1})])]}),makeQuery(id+"FV6EzTKN9YXR9Vd_1.opExtrude","SWEPT_FACE",FACE,{"disambiguationData":[OSD([subQ1]),TDD([makeQuery(id+"F37MvCQ3r0wqFin_1.imprint","IMPRINT",EDGE,{"disambiguationData":[TD([[makeQuery(id+"F37MvCQ3r0wqFin_1.imprint","INTERSECT",VERTEX,{"disambiguationData":[OD(0.0)],"derivedFrom":[subQ1,subQ3]}),-1.0]])],"derivedFrom":subQ1})])]}),makeQuery(id+"FV6EzTKN9YXR9Vd_1.opExtrude","SWEPT_FACE",FACE,{"disambiguationData":[OSD([subQ1]),TDD([makeQuery(id+"F37MvCQ3r0wqFin_1.imprint","IMPRINT",EDGE,{"disambiguationData":[TD([[makeQuery(id+"F37MvCQ3r0wqFin_1.imprint","INTERSECT",VERTEX,{"disambiguationData":[OD(1.0)],"derivedFrom":[subQ1,subQ3]}),1.0]])],"derivedFrom":subQ1})])]}),makeQuery(id+"FV6EzTKN9YXR9Vd_1.opExtrude","SWEPT_FACE",FACE,{"disambiguationData":[OSD([subQ1]),TDD([makeQuery(id+"F37MvCQ3r0wqFin_1.imprint","IMPRINT",EDGE,{"disambiguationData":[TD([[makeQuery(id+"F37MvCQ3r0wqFin_1.imprint","INTERSECT",VERTEX,{"disambiguationData":[OD(1.0)],"derivedFrom":[subQ1,subQ0]}),1.0]])],"derivedFrom":subQ1})])]}),makeQuery(id+"FV6EzTKN9YXR9Vd_1.opExtrude","SWEPT_FACE",FACE,{"disambiguationData":[OSD([subQ1]),TDD([makeQuery(id+"F37MvCQ3r0wqFin_1.imprint","IMPRINT",EDGE,{"disambiguationData":[TD([[makeQuery(id+"F37MvCQ3r0wqFin_1.imprint","INTERSECT",VERTEX,{"disambiguationData":[OD(1.0)],"derivedFrom":[subQ1,subQ6]}),-1.0]])],"derivedFrom":subQ1})])]}),makeQuery(id+"FV6EzTKN9YXR9Vd_1.opExtrude","SWEPT_FACE",FACE,{"disambiguationData":[OSD([subQ1]),TDD([makeQuery(id+"F37MvCQ3r0wqFin_1.imprint","IMPRINT",EDGE,{"disambiguationData":[TD([[makeQuery(id+"F37MvCQ3r0wqFin_1.imprint","INTERSECT",VERTEX,{"disambiguationData":[OD(1.0)],"derivedFrom":[subQ1,subQ8]}),-1.0]])],"derivedFrom":subQ1})])]}),makeQuery(id+"FV6EzTKN9YXR9Vd_1.opExtrude","SWEPT_FACE",FACE,{"disambiguationData":[OSD([subQ1]),TDD([makeQuery(id+"F37MvCQ3r0wqFin_1.imprint","IMPRINT",EDGE,{"disambiguationData":[TD([[makeQuery(id+"F37MvCQ3r0wqFin_1.imprint","INTERSECT",VERTEX,{"disambiguationData":[OD(1.0)],"derivedFrom":[subQ1,subQ10]}),-1.0]])],"derivedFrom":subQ1})])]}),makeQuery(id+"FV6EzTKN9YXR9Vd_1.opExtrude","SWEPT_FACE",FACE,{"disambiguationData":[OSD([subQ7])]}),makeQuery(id+"FV6EzTKN9YXR9Vd_1.opExtrude","SWEPT_FACE",FACE,{"disambiguationData":[OSD([subQ8])]})]),OD(1.0)],"derivedFrom":makeQuery(id+"F1.opExtrude","CAP_EDGE",EDGE,{"disambiguationData":[OSD([subQ5])],"isStart":false})});}
            var Q8;
            {var subQ0=sQuery(id+"F37MvCQ3r0wqFin_1.wireOp",EDGE,"f4uybqiO-2By2-jBmk-46SA-pqxdGsBmxj9X");var subQ1=sQuery(id+"F37MvCQ3r0wqFin_1.wireOp",EDGE,"YBS4xQga-kdXz-Xd6Z-IQxe-r2HOvKNWWecW");var subQ3=sQuery(id+"F37MvCQ3r0wqFin_1.wireOp",EDGE,"gupYa68e-aYtB-tSWe-53kB-uYkL865cLbxZ");var subQ5=sQuery(id+"F0.wireOp",EDGE,"E0");var subQ6=sQuery(id+"F37MvCQ3r0wqFin_1.wireOp",EDGE,"S5JysFVE-GN5k-qked-gyNs-9rrJIgPoBisO");var subQ8=sQuery(id+"F37MvCQ3r0wqFin_1.wireOp",EDGE,"622e7514-f5f2-47ed-ba9b-ec6ca30ba75c0.MirrorCS");var subQ10=sQuery(id+"F37MvCQ3r0wqFin_1.wireOp",EDGE,"19809d41-3397-4dab-8baa-fab7fa50255a0.MirrorCS");Q8=makeQuery(id+"FV6EzTKN9YXR9Vd_1.boolean.opBoolean","SPLIT",EDGE,{"disambiguationData":[TD([makeQuery(id+"F1.opExtrude","SWEPT_FACE",FACE,{"disambiguationData":[OSD([subQ5])]}),makeQuery(id+"F1.opExtrude","CAP_FACE",FACE,{"disambiguationData":[OSD([subQ5])],"isStart":false}),makeQuery(id+"FV6EzTKN9YXR9Vd_1.opExtrude","SWEPT_FACE",FACE,{"disambiguationData":[OSD([subQ1]),TDD([makeQuery(id+"F37MvCQ3r0wqFin_1.imprint","IMPRINT",EDGE,{"disambiguationData":[TD([[makeQuery(id+"F37MvCQ3r0wqFin_1.imprint","INTERSECT",VERTEX,{"disambiguationData":[OD(0.0)],"derivedFrom":[subQ1,subQ10]}),1.0]])],"derivedFrom":subQ1})])]}),makeQuery(id+"FV6EzTKN9YXR9Vd_1.opExtrude","SWEPT_FACE",FACE,{"disambiguationData":[OSD([subQ1]),TDD([makeQuery(id+"F37MvCQ3r0wqFin_1.imprint","IMPRINT",EDGE,{"disambiguationData":[TD([[makeQuery(id+"F37MvCQ3r0wqFin_1.imprint","INTERSECT",VERTEX,{"disambiguationData":[OD(0.0)],"derivedFrom":[subQ1,subQ8]}),1.0]])],"derivedFrom":subQ1})])]}),makeQuery(id+"FV6EzTKN9YXR9Vd_1.opExtrude","SWEPT_FACE",FACE,{"disambiguationData":[OSD([subQ1]),TDD([makeQuery(id+"F37MvCQ3r0wqFin_1.imprint","IMPRINT",EDGE,{"disambiguationData":[TD([[makeQuery(id+"F37MvCQ3r0wqFin_1.imprint","INTERSECT",VERTEX,{"disambiguationData":[OD(0.0)],"derivedFrom":[subQ1,subQ6]}),1.0]])],"derivedFrom":subQ1})])]}),makeQuery(id+"FV6EzTKN9YXR9Vd_1.opExtrude","SWEPT_FACE",FACE,{"disambiguationData":[OSD([subQ1]),TDD([makeQuery(id+"F37MvCQ3r0wqFin_1.imprint","IMPRINT",EDGE,{"disambiguationData":[TD([[makeQuery(id+"F37MvCQ3r0wqFin_1.imprint","INTERSECT",VERTEX,{"disambiguationData":[OD(0.0)],"derivedFrom":[subQ1,subQ0]}),-1.0]])],"derivedFrom":subQ1})])]}),makeQuery(id+"FV6EzTKN9YXR9Vd_1.opExtrude","SWEPT_FACE",FACE,{"disambiguationData":[OSD([subQ1]),TDD([makeQuery(id+"F37MvCQ3r0wqFin_1.imprint","IMPRINT",EDGE,{"disambiguationData":[TD([[makeQuery(id+"F37MvCQ3r0wqFin_1.imprint","INTERSECT",VERTEX,{"disambiguationData":[OD(0.0)],"derivedFrom":[subQ1,subQ3]}),-1.0]])],"derivedFrom":subQ1})])]}),makeQuery(id+"FV6EzTKN9YXR9Vd_1.opExtrude","SWEPT_FACE",FACE,{"disambiguationData":[OSD([subQ1]),TDD([makeQuery(id+"F37MvCQ3r0wqFin_1.imprint","IMPRINT",EDGE,{"disambiguationData":[TD([[makeQuery(id+"F37MvCQ3r0wqFin_1.imprint","INTERSECT",VERTEX,{"disambiguationData":[OD(1.0)],"derivedFrom":[subQ1,subQ3]}),1.0]])],"derivedFrom":subQ1})])]}),makeQuery(id+"FV6EzTKN9YXR9Vd_1.opExtrude","SWEPT_FACE",FACE,{"disambiguationData":[OSD([subQ1]),TDD([makeQuery(id+"F37MvCQ3r0wqFin_1.imprint","IMPRINT",EDGE,{"disambiguationData":[TD([[makeQuery(id+"F37MvCQ3r0wqFin_1.imprint","INTERSECT",VERTEX,{"disambiguationData":[OD(1.0)],"derivedFrom":[subQ1,subQ0]}),1.0]])],"derivedFrom":subQ1})])]}),makeQuery(id+"FV6EzTKN9YXR9Vd_1.opExtrude","SWEPT_FACE",FACE,{"disambiguationData":[OSD([subQ1]),TDD([makeQuery(id+"F37MvCQ3r0wqFin_1.imprint","IMPRINT",EDGE,{"disambiguationData":[TD([[makeQuery(id+"F37MvCQ3r0wqFin_1.imprint","INTERSECT",VERTEX,{"disambiguationData":[OD(1.0)],"derivedFrom":[subQ1,subQ6]}),-1.0]])],"derivedFrom":subQ1})])]}),makeQuery(id+"FV6EzTKN9YXR9Vd_1.opExtrude","SWEPT_FACE",FACE,{"disambiguationData":[OSD([subQ1]),TDD([makeQuery(id+"F37MvCQ3r0wqFin_1.imprint","IMPRINT",EDGE,{"disambiguationData":[TD([[makeQuery(id+"F37MvCQ3r0wqFin_1.imprint","INTERSECT",VERTEX,{"disambiguationData":[OD(1.0)],"derivedFrom":[subQ1,subQ8]}),-1.0]])],"derivedFrom":subQ1})])]}),makeQuery(id+"FV6EzTKN9YXR9Vd_1.opExtrude","SWEPT_FACE",FACE,{"disambiguationData":[OSD([subQ1]),TDD([makeQuery(id+"F37MvCQ3r0wqFin_1.imprint","IMPRINT",EDGE,{"disambiguationData":[TD([[makeQuery(id+"F37MvCQ3r0wqFin_1.imprint","INTERSECT",VERTEX,{"disambiguationData":[OD(1.0)],"derivedFrom":[subQ1,subQ10]}),-1.0]])],"derivedFrom":subQ1})])]}),makeQuery(id+"FV6EzTKN9YXR9Vd_1.opExtrude","SWEPT_FACE",FACE,{"disambiguationData":[OSD([subQ6])]}),makeQuery(id+"FV6EzTKN9YXR9Vd_1.opExtrude","SWEPT_FACE",FACE,{"disambiguationData":[OSD([subQ0])]})]),OD(1.0)],"derivedFrom":makeQuery(id+"F1.opExtrude","CAP_EDGE",EDGE,{"disambiguationData":[OSD([subQ5])],"isStart":false})});}
            var Q9;
            {var subQ0=sQuery(id+"F37MvCQ3r0wqFin_1.wireOp",EDGE,"f4uybqiO-2By2-jBmk-46SA-pqxdGsBmxj9X");var subQ1=sQuery(id+"F37MvCQ3r0wqFin_1.wireOp",EDGE,"YBS4xQga-kdXz-Xd6Z-IQxe-r2HOvKNWWecW");var subQ2=sQuery(id+"F37MvCQ3r0wqFin_1.wireOp",EDGE,"x8pBDlyB-b0kH-kFwn-oj1M-qMSimfXZpj5B");var subQ3=sQuery(id+"F37MvCQ3r0wqFin_1.wireOp",EDGE,"gupYa68e-aYtB-tSWe-53kB-uYkL865cLbxZ");var subQ5=sQuery(id+"F0.wireOp",EDGE,"E0");var subQ6=sQuery(id+"F37MvCQ3r0wqFin_1.wireOp",EDGE,"S5JysFVE-GN5k-qked-gyNs-9rrJIgPoBisO");var subQ8=sQuery(id+"F37MvCQ3r0wqFin_1.wireOp",EDGE,"622e7514-f5f2-47ed-ba9b-ec6ca30ba75c0.MirrorCS");var subQ10=sQuery(id+"F37MvCQ3r0wqFin_1.wireOp",EDGE,"19809d41-3397-4dab-8baa-fab7fa50255a0.MirrorCS");Q9=makeQuery(id+"FV6EzTKN9YXR9Vd_1.boolean.opBoolean","SPLIT",EDGE,{"disambiguationData":[TD([makeQuery(id+"F1.opExtrude","SWEPT_FACE",FACE,{"disambiguationData":[OSD([subQ5])]}),makeQuery(id+"F1.opExtrude","CAP_FACE",FACE,{"disambiguationData":[OSD([subQ5])],"isStart":false}),makeQuery(id+"FV6EzTKN9YXR9Vd_1.opExtrude","SWEPT_FACE",FACE,{"disambiguationData":[OSD([subQ1]),TDD([makeQuery(id+"F37MvCQ3r0wqFin_1.imprint","IMPRINT",EDGE,{"disambiguationData":[TD([[makeQuery(id+"F37MvCQ3r0wqFin_1.imprint","INTERSECT",VERTEX,{"disambiguationData":[OD(0.0)],"derivedFrom":[subQ1,subQ10]}),1.0]])],"derivedFrom":subQ1})])]}),makeQuery(id+"FV6EzTKN9YXR9Vd_1.opExtrude","SWEPT_FACE",FACE,{"disambiguationData":[OSD([subQ1]),TDD([makeQuery(id+"F37MvCQ3r0wqFin_1.imprint","IMPRINT",EDGE,{"disambiguationData":[TD([[makeQuery(id+"F37MvCQ3r0wqFin_1.imprint","INTERSECT",VERTEX,{"disambiguationData":[OD(0.0)],"derivedFrom":[subQ1,subQ8]}),1.0]])],"derivedFrom":subQ1})])]}),makeQuery(id+"FV6EzTKN9YXR9Vd_1.opExtrude","SWEPT_FACE",FACE,{"disambiguationData":[OSD([subQ1]),TDD([makeQuery(id+"F37MvCQ3r0wqFin_1.imprint","IMPRINT",EDGE,{"disambiguationData":[TD([[makeQuery(id+"F37MvCQ3r0wqFin_1.imprint","INTERSECT",VERTEX,{"disambiguationData":[OD(0.0)],"derivedFrom":[subQ1,subQ6]}),1.0]])],"derivedFrom":subQ1})])]}),makeQuery(id+"FV6EzTKN9YXR9Vd_1.opExtrude","SWEPT_FACE",FACE,{"disambiguationData":[OSD([subQ1]),TDD([makeQuery(id+"F37MvCQ3r0wqFin_1.imprint","IMPRINT",EDGE,{"disambiguationData":[TD([[makeQuery(id+"F37MvCQ3r0wqFin_1.imprint","INTERSECT",VERTEX,{"disambiguationData":[OD(0.0)],"derivedFrom":[subQ1,subQ0]}),-1.0]])],"derivedFrom":subQ1})])]}),makeQuery(id+"FV6EzTKN9YXR9Vd_1.opExtrude","SWEPT_FACE",FACE,{"disambiguationData":[OSD([subQ1]),TDD([makeQuery(id+"F37MvCQ3r0wqFin_1.imprint","IMPRINT",EDGE,{"disambiguationData":[TD([[makeQuery(id+"F37MvCQ3r0wqFin_1.imprint","INTERSECT",VERTEX,{"disambiguationData":[OD(0.0)],"derivedFrom":[subQ1,subQ3]}),-1.0]])],"derivedFrom":subQ1})])]}),makeQuery(id+"FV6EzTKN9YXR9Vd_1.opExtrude","SWEPT_FACE",FACE,{"disambiguationData":[OSD([subQ1]),TDD([makeQuery(id+"F37MvCQ3r0wqFin_1.imprint","IMPRINT",EDGE,{"disambiguationData":[TD([[makeQuery(id+"F37MvCQ3r0wqFin_1.imprint","INTERSECT",VERTEX,{"disambiguationData":[OD(1.0)],"derivedFrom":[subQ1,subQ3]}),1.0]])],"derivedFrom":subQ1})])]}),makeQuery(id+"FV6EzTKN9YXR9Vd_1.opExtrude","SWEPT_FACE",FACE,{"disambiguationData":[OSD([subQ1]),TDD([makeQuery(id+"F37MvCQ3r0wqFin_1.imprint","IMPRINT",EDGE,{"disambiguationData":[TD([[makeQuery(id+"F37MvCQ3r0wqFin_1.imprint","INTERSECT",VERTEX,{"disambiguationData":[OD(1.0)],"derivedFrom":[subQ1,subQ0]}),1.0]])],"derivedFrom":subQ1})])]}),makeQuery(id+"FV6EzTKN9YXR9Vd_1.opExtrude","SWEPT_FACE",FACE,{"disambiguationData":[OSD([subQ1]),TDD([makeQuery(id+"F37MvCQ3r0wqFin_1.imprint","IMPRINT",EDGE,{"disambiguationData":[TD([[makeQuery(id+"F37MvCQ3r0wqFin_1.imprint","INTERSECT",VERTEX,{"disambiguationData":[OD(1.0)],"derivedFrom":[subQ1,subQ6]}),-1.0]])],"derivedFrom":subQ1})])]}),makeQuery(id+"FV6EzTKN9YXR9Vd_1.opExtrude","SWEPT_FACE",FACE,{"disambiguationData":[OSD([subQ1]),TDD([makeQuery(id+"F37MvCQ3r0wqFin_1.imprint","IMPRINT",EDGE,{"disambiguationData":[TD([[makeQuery(id+"F37MvCQ3r0wqFin_1.imprint","INTERSECT",VERTEX,{"disambiguationData":[OD(1.0)],"derivedFrom":[subQ1,subQ8]}),-1.0]])],"derivedFrom":subQ1})])]}),makeQuery(id+"FV6EzTKN9YXR9Vd_1.opExtrude","SWEPT_FACE",FACE,{"disambiguationData":[OSD([subQ1]),TDD([makeQuery(id+"F37MvCQ3r0wqFin_1.imprint","IMPRINT",EDGE,{"disambiguationData":[TD([[makeQuery(id+"F37MvCQ3r0wqFin_1.imprint","INTERSECT",VERTEX,{"disambiguationData":[OD(1.0)],"derivedFrom":[subQ1,subQ10]}),-1.0]])],"derivedFrom":subQ1})])]}),makeQuery(id+"FV6EzTKN9YXR9Vd_1.opExtrude","SWEPT_FACE",FACE,{"disambiguationData":[OSD([subQ2])]}),makeQuery(id+"FV6EzTKN9YXR9Vd_1.opExtrude","SWEPT_FACE",FACE,{"disambiguationData":[OSD([subQ3])]})]),OD(1.0)],"derivedFrom":makeQuery(id+"F1.opExtrude","CAP_EDGE",EDGE,{"disambiguationData":[OSD([subQ5])],"isStart":false})});}
            fillet(context, id + "F2", {"entities" : qUnion([Q0, Q1, Q2, Q3, Q4, Q5, Q6, Q7, Q8, Q9]), "radius" : 2 * mm, "tangentPropagation" : true, "allowEdgeOverflow" : false});
        }
        {
            var Q0;
            Q0=makeQuery(id+"F1.opExtrude","CAP_FACE",FACE,{"disambiguationData":[OSD([sQuery(id+"F0.wireOp",EDGE,"E0")])],"isStart":true});
            var sketch = newSketch(context, id + "F3", { "sketchPlane" : qUnion([Q0])});
            skLineSegment(sketch, "E1", {"start": v(0, 42.36) * mm, "end": v(0, -39.62) * mm, "construction": true});
            skCircle(sketch, "E2", {"center": v(0, 13) * mm, "radius": 1.5 * mm});
            skLineSegment(sketch, "E3", {"start": v(0, 0) * mm, "end": v(-17.75, 0) * mm, "construction": true});
            skCircle(sketch, "E4.MirrorC", {"center": v(0, -13) * mm, "radius": 1.5 * mm});
            skSolve(sketch);
        }
        {
            var Q0;
            Q0=makeQuery(id+"F3.imprint","IMPRINT",FACE,{"disambiguationData":[TD([[makeQuery(id+"F3.imprint","IMPRINT",EDGE,{"derivedFrom":sQuery(id+"F3.wireOp",EDGE,"E2")}),1.0]])]});
            var Q1;
            Q1=makeQuery(id+"F3.imprint","IMPRINT",FACE,{"disambiguationData":[TD([[makeQuery(id+"F3.imprint","IMPRINT",EDGE,{"derivedFrom":sQuery(id+"F3.wireOp",EDGE,"E4.MirrorC")}),-1.0]])]});
            extrude(context, id + "F4", {"entities" : qUnion([Q0, Q1]), "operationType" : NewBodyOperationType.REMOVE, "endBound" : BoundingType.THROUGH_ALL, "oppositeDirection" : true, "depth" : 25 * mm, "offsetDistance" : 25 * mm});
        }
    });
